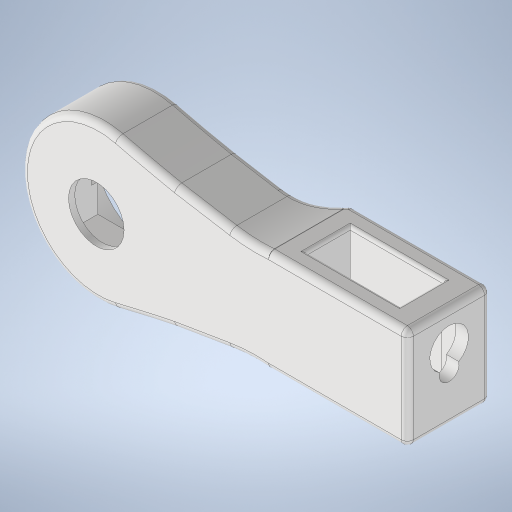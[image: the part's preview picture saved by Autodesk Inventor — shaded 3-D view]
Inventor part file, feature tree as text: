
AUTODESK INVENTOR PART (.ipt)
format: ipt  version: 2024 (Build 280153000, 153)  size: 979,456 bytes
history: native  units: mm
features: extrude x11, projected_geometry x9, plane x6, fillet x6, other x6, reference x3, mirror x2
ambient origin geometry x8: Origin, YZ Plane, XZ Plane, XY Plane, X Axis, Y Axis, Z Axis, Center Point
bodies: Solid1 (feature_tree)
feature tree (43):
  plane  "Work Plane1"
  extrude  "Extrusion1"  Depth=40.25mm
  extrude  "Extrusion2"  Depth=20.25mm
  plane  "Work Plane2"
  extrude  "Extrusion3"  TaperAngle=0.0deg  [1 undecoded]
  mirror  "Mirror2"
  extrude  "Extrusion4"  Depth=40.25mm
  extrude  "Extrusion6"  Depth=50.0mm
  fillet  "Fillet1"  Radius=55.0mm
  extrude  "Extrusion7"  Depth=15.0mm
  extrude  "Extrusion8"  Depth=15.0mm
  extrude  "Extrusion9"  Depth=20.0mm
  extrude  "Extrusion10"  Depth=20.0mm
  plane  "Work Plane3"
  fillet  "Fillet7"  Radius=12.817996mm
  fillet  "Fillet8"  Radius=12.817996mm
  fillet  "Fillet10"  Radius=8.0mm
  extrude  "Extrusion12"  Depth=10.125mm
  fillet  "Fillet15"  Radius=5.5mm
  fillet  "Fillet16"  Radius=1.0mm
  extrude  "Extrusion15"  Depth=1.0mm
  plane  "Work Plane7"
  plane  "Work Plane8"
  plane  "Work Plane9"
  mirror  "Mirror5"
  reference  "Reference1"
  reference  "Reference2"
  reference  "Reference3"
  projected_geometry  "Projected Loop1"
  projected_geometry  "Projected Loop2"
  projected_geometry  "Projected Loop3"
  projected_geometry  "Projected Loop5"
  projected_geometry  "Projected Loop7"
  projected_geometry  "Projected Loop8"
  projected_geometry  "Projected Loop10"
  projected_geometry  "Projected Loop12"
  projected_geometry  "Projected Loop14"
  other  "<userpath> windows\Documents\Inventor\Robotska_roka\Assembly4.iam"
  other  "Assembly4.iam"
  other  "Servo Motor MG996R  With Attachments:5"
  other  "servoMotorMG996R_7"
  other  "Servo Motor MG996R  With Attachments:6"
  other  "attachmentCircular_1"
note: 1 required parameter value undecoded (feature->parameter linkage not recoverable at this tier; creation-order binding heuristic only, values carry confidence <= 0.55)
